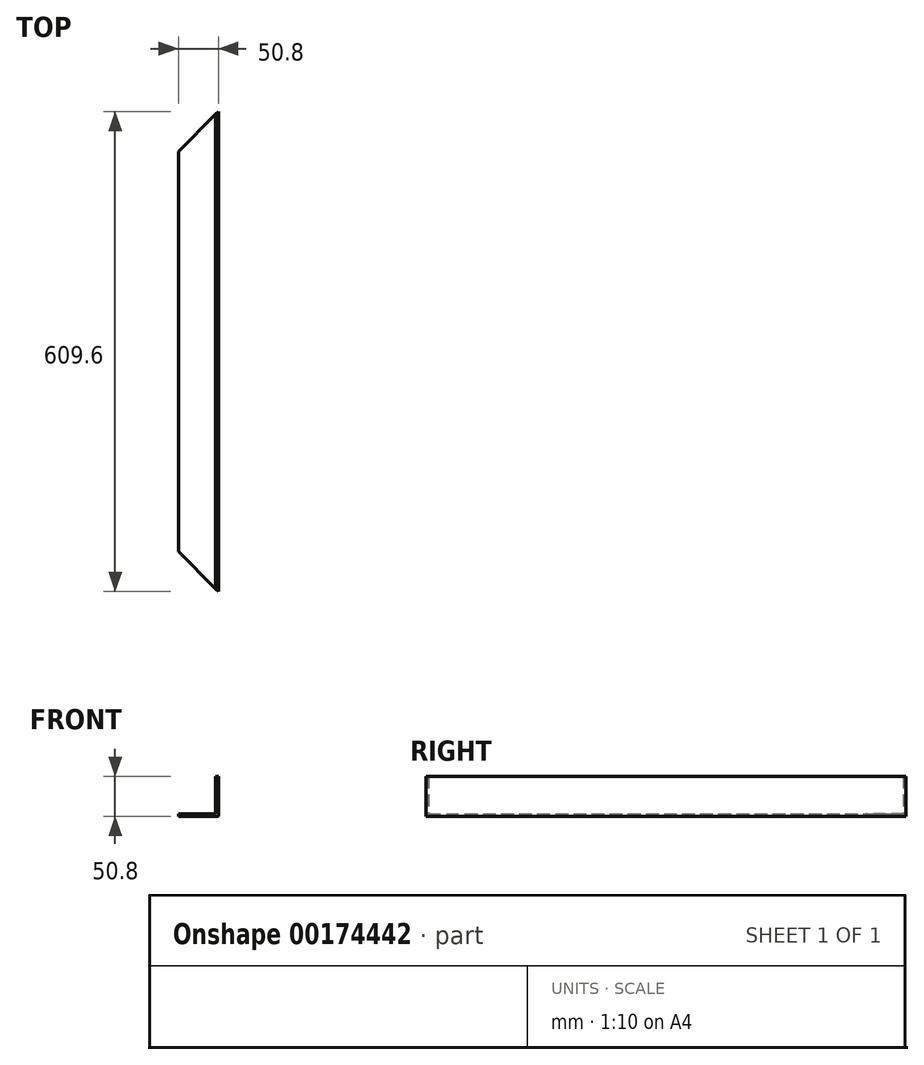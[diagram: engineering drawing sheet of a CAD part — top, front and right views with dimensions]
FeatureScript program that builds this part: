
annotation { "Feature Type Name" : "Feature", "Feature Type Description" : "" }
export const myFeature = defineFeature(function(context is Context, id is Id, definition is map)
    precondition{}
    {
        {
            var Q0;
            Q0=qCreatedBy(makeId("Front.planeOp"),FACE);
            var sketch = newSketch(context, id + "F0", { "sketchPlane" : qUnion([Q0])});
            skLineSegment(sketch, "E0.bottom", {"start": v(76.2, 0) * mm, "end": v(127, 0) * mm});
            skLineSegment(sketch, "E0.top", {"start": v(76.2, 3.18) * mm, "end": v(123.83, 3.18) * mm});
            skLineSegment(sketch, "E0.left", {"start": v(76.2, 0) * mm, "end": v(76.2, 3.18) * mm});
            skLineSegment(sketch, "E1.top", {"start": v(127, 50.8) * mm, "end": v(123.82, 50.8) * mm});
            skLineSegment(sketch, "E1.left", {"start": v(127, 0) * mm, "end": v(127, 50.8) * mm});
            skLineSegment(sketch, "E2", {"start": v(123.83, 3.18) * mm, "end": v(123.83, 50.8) * mm});
            skSolve(sketch);
        }
        {
            var Q0;
            Q0 = qSketchRegion(id + "F0", true);
            extrude(context, id + "F1", {"entities" : qUnion([Q0]), "endBound" : BoundingType.SYMMETRIC, "depth" : 609.6 * mm});
        }
        {
            var Q0;
            Q0=makeQuery(id+"F1.opExtrude","CAP_EDGE",EDGE,{"disambiguationData":[OSD([sQuery(id+"F0.wireOp",EDGE,"E0.left")])],"isStart":false});
            chamfer(context, id + "F2", {"entities" : qUnion([Q0]), "width" : 50.8 * mm, "tangentPropagation" : true});
        }
        {
            var Q0;
            Q0=makeQuery(id+"F1.opExtrude","CAP_EDGE",EDGE,{"disambiguationData":[OSD([sQuery(id+"F0.wireOp",EDGE,"E0.left")])],"isStart":true});
            chamfer(context, id + "F3", {"entities" : qUnion([Q0]), "width" : 50.8 * mm, "tangentPropagation" : true});
        }
    });
